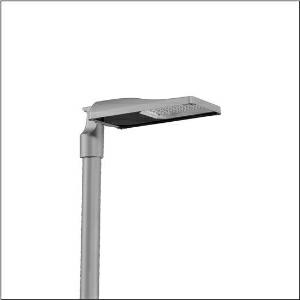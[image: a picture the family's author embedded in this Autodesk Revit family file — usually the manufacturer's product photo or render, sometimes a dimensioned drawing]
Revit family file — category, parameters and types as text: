
# Revit family: streetlight_sl_31_mini___st1_0a_5xh2d31b08ja_82e6
name_source: partatom
category: Lighting Fixtures
units: mm (PartAtom-declared; Revit-internal decimal feet)

## family parameters
Cut with Voids When Loaded = No
Host = Face
Light Source = No
Part Type = Normal
Room Calculation Point = No
Round Connector Dimension = Use Diameter
Shared = No

## types (1)
- --- (1 x LED, 12140 lm, 81.1 W, 3000K)
    Apparent Load = 81 VA
    CIE Flux Codes = 40 73 97 100 100
    Color Rendering = 70
    Color Temperature = 3000K
    Default Elevation = 1800 mm
    Description = Streetlight SL 31 mini Easy, LST, Desk-Remote mast luminaire for post-top, side-entry; light control with lens of PMMA; light distribution: ST1.0a, direct asymmetric distribution, for standard-compliant lighting for roads and squares; LED: luminous flux: 12.140lm, light colour: 730, colour temperature: 3000K; luminous efficacy: 149,7lm/W; control: pre-setting: linear dimming characteristic, flexible luminous flux parameterisation, time-dependent luminous flux control, constant luminous flux control, power reduction, intelligent temperature release in ECG and LED module, overheat protection; luminaire housing, of diecast aluminium, SITECO metallic grey (DB 702S), corrosivity category C5 high according to DIN EN ISO 12944; cover of toughened safety glass, transparent, mast flange of diecast aluminium, SITECO metallic grey (DB 702S), spigot size: 76/60mm, mast flange included unmounted; with cable H07RN-F 5x 1.5mm², cable length: 10,5m, connection cable pre-assembled; mains connection: 220..240V, AC, 50/60Hz; power consumption (at start of service life): 81,1W / (at end of service life): 88,3W / (with reduced operation 50%): 36,4W; protection rating (complete): IP66; insulation class (complete): insulation class II (safety insulation); impact resistance: IK10; certification: CE, ENEC, ENEC+, VDE, UKCA; permissible operating ambient temperature for outdoor applications: -40..+50°C; packaging unit: 1 piece

Light Distribution: ST1.0a
    Height = 76 mm
    Lamp = 1 x LED
    Lamp Light Flux = 12140 lm
    Lamp Power = 81.1 W
    Lamp count = 1
    Length = 547 mm
    Luminous efficacy = 150 lm/W
    Manufacturer = Siteco
    ModVariant = No
    Model = 5XH2D31B08JA
    Number of Poles = 1
    OnlyDefault = Yes
    Power Factor = 1
    Product Name = Streetlight SL 31 mini | ST1.0a
    Product group = mast luminaire | pylon top
    ProductGroupID = 6100
    Protection Class = Protection class II
    Protection Degree = IP 66
    RLX_Detail_Level = 1
    RLX_Emergency_Light_Flux = 0 lm
    RLX_Emergency_Type = 0
    RLX_Emergency_Type_DB = No
    RlxData = <blob elided: 39657 chars, md5=b7eca3e7>
    Socket = socket
    Standby Power = 0 W
    System Light Flux = 12140 lm
    System Power = 81 W
    Type Comments = factory setting: luminous flux: 100 % | dim-lin: 254 | 860 mA
    Type Image = l_1300326.jpg
    URL = http://relux.com
    VarID = @adj_057875
    Voltage = 0 V
    Weight = 0.00 kg
    Width = 265 mm

## geometry (parser evidence)
native form markers: Blend x4, Sweep x9
no freeform markers — native parametric forms only
